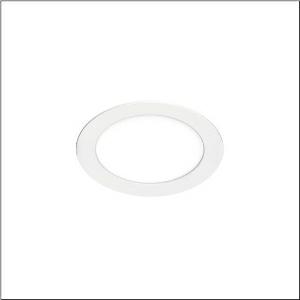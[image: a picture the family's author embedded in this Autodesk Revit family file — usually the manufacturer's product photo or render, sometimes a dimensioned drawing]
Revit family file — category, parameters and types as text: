
# Revit family: lunis_41_flat_51dr107fhca
name_source: partatom
category: Lighting Fixtures
units: mm (PartAtom-declared; Revit-internal decimal feet)

## family parameters
Cut with Voids When Loaded = No
Host = Face
Light Source = No
Part Type = Normal
Room Calculation Point = No
Round Connector Dimension = Use Diameter
Shared = No

## types (1)
- --- (1 x LED, 2160 lm, 22 W, 5700K)
    Apparent Load = 22 VA
    CIE Flux Codes = 49 80 96 100 100
    Color Rendering = 80
    Color Temperature = 5700K
    Default Elevation = 1800 mm
    Description = Lunis 41,  flat, downlight, light emission: direct distribution, LED rated luminous flux: 2.160lm, light colour: 840/857, control gear: ECG, mains connection: 230V, AC, 50/60Hz, housing, round, of aluminium, coated, traffic white (RAL 9016), diameter: 225mm, protection rating (complete): IP20, insulation class (complete): insulation class II (safety insulation), certification: CE, permissible ambient temperature for indoor applications: -20..+40°C, packaging unit: 1 piece
    Height = 0 mm  [stored 0 ft]
    Lamp = 1 x LED
    Lamp Light Flux = 2160 lm
    Lamp Power = 22 W
    Lamp count = 1
    Length = 225 mm
    Luminous efficacy = 98 lm/W
    Manufacturer = Siteco
    ModVariant = No
    Model = 51DR107FHCA
    Mounting Place = Ceiling
    Mounting Type = Recessed
    Number of Poles = 1
    OnlyDefault = Yes
    Power Factor = 1
    Product Name = Lunis 41 flat
    Product group = downlight | ceiling recessed
    ProductGroupID = 402
    Protection Class = Protection class II
    Protection Degree = IP 20
    RLX_Detail_Level = 1
    RlxData = <blob elided: 22145 chars, md5=b2c6e88d>
    Socket = socket
    Standby Power = 0 W
    System Light Flux = 2160 lm
    System Power = 22 W
    Type Comments = factory setting: colour temperature 5700K
    Type Image = l_1007032.jpg
    URL = http://relux.com
    VarID = @adj_117309
    Voltage = 0 V
    Weight = 0.00 kg
    Width = 0 mm  [stored 0 ft]

note: [stored X ft] marks values corroborated as IEEE doubles in the binary element streams (Revit-internal decimal feet)

## geometry (parser evidence)
native form markers: Blend x4, Sweep x12
no freeform markers — native parametric forms only
